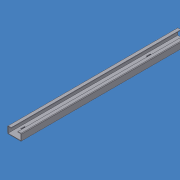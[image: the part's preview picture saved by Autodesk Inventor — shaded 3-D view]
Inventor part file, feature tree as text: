
AUTODESK INVENTOR PART (.ipt)
format: ipt  version: 2015 (Build 190159000, 159)  size: 246,272 bytes
history: native  units: mm
features: sheet_metal_op x9, other x8, sketch x6, plane x2
ambient origin geometry x8: Origin, YZ Plane, XZ Plane, XY Plane, X Axis, Y Axis, Z Axis, Center Point
bodies: Solid1 (feature_tree)
feature tree (25):
  sheet_metal_op  "Face1"
  sheet_metal_op  "Flange1"
  sheet_metal_op  "Flange2"
  sheet_metal_op  "Flange3"
  sheet_metal_op  "Flange4"
  plane  "Work Plane4"
  plane  "Work Plane6"
  sketch  "Sketch1"  dims[d4=0.001mm]
  other  "Plate1"
  sketch  "Sketch2"  dims[d5=3.0mm]
  other  "Plate2"
  sheet_metal_op  "Bend1"
  sketch  "Sketch3"  dims[d6=0.001mm]
  other  "Plate3"
  sheet_metal_op  "Bend2"
  sketch  "Sketch4"  dims[d7=6.0mm]
  other  "Plate4"
  sheet_metal_op  "Bend3"
  sketch  "Sketch5"  dims[d8=0.001mm]
  other  "Plate5"
  sheet_metal_op  "Bend4"
  sketch  "Sketch6"  dims[d9=29.0mm d10=90.0deg d11=0.001mm d12=3.0mm d13=0.001mm d14=6.0mm d15=0.001mm d16=29.0mm d17=90.0deg d18=0.001mm d19=3.0mm d20=0.001mm d21=6.0mm d22=0.001mm d23=15.0mm d24=90.0deg d25=0.001mm d26=3.0mm d27=0.001mm d28=6.0mm d29=0.001mm d30=15.0mm d31=90.0deg d32=0.001mm d33=4.0mm d34=20.5mm d35=4.0mm d36=20.5mm d37=0.0mm d38=33.0mm d40=4.0mm d41=0.0mm d42=850.0mm d45=150.0mm d46=10.0mm d47=10.0mm d48=64.0mm d49=6.0mm d50=64.0mm d51=4.0mm d52=9.0mm d62=20.5mm d63=4.0mm d64=9.0mm d65=20.5mm d66=4.0mm d68=4.0mm d69=0.0mm d71=50.0mm d72=33.0mm d73=16.5mm d0=3.0mm]
  other  "FlatPattern"
  other  "Cut1"
  other  "FlatPatternExtrusion2"
